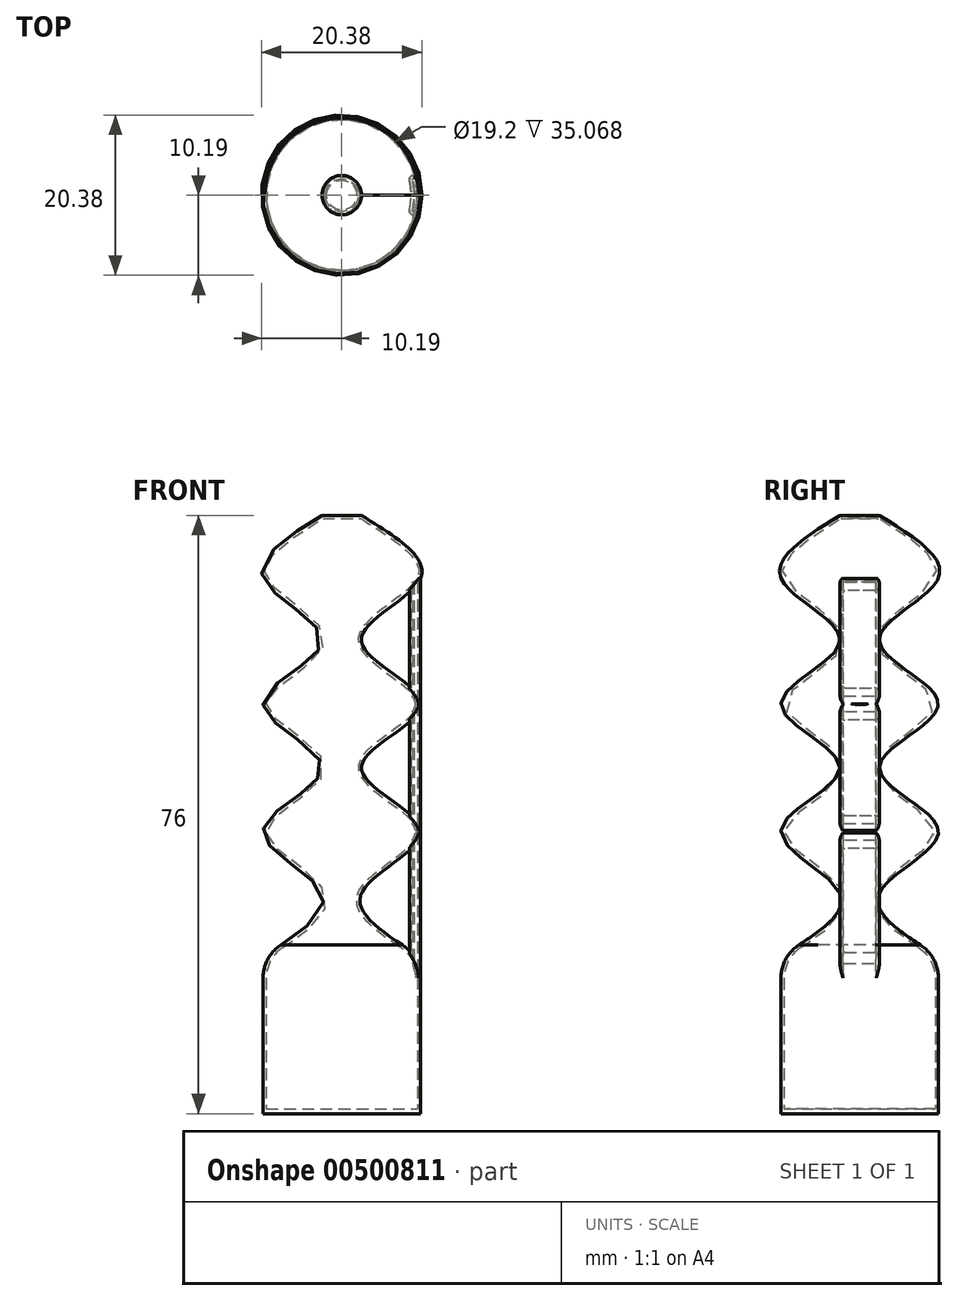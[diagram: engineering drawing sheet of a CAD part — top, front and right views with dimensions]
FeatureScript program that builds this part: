
annotation { "Feature Type Name" : "Feature", "Feature Type Description" : "" }
export const myFeature = defineFeature(function(context is Context, id is Id, definition is map)
    precondition{}
    {
        {
            var Q0;
            Q0=qCreatedBy(makeId("Top.planeOp"),FACE);
            var sketch = newSketch(context, id + "F0", { "sketchPlane" : qUnion([Q0])});
            skCircle(sketch, "E0", {"center": v(0, 0) * mm, "radius": 10 * mm});
            skSolve(sketch);
        }
        {
            var Q0;
            Q0 = qSketchRegion(id + "F0", true);
            extrude(context, id + "F1", {"entities" : qUnion([Q0]), "depth" : 20 * mm, "offsetDistance" : 25 * mm});
        }
        {
            var Q0;
            Q0=qCreatedBy(makeId("Top.planeOp"),FACE);
            cPlane(context, id + "F2", {"entities" : qUnion([Q0]), "cplaneType" : CPlaneType.OFFSET, "offset" : 20 * mm, "width" : 150 * mm, "height" : 150 * mm});
        }
        {
            var Q0;
            Q0=qCreatedBy(id+"F2.planeOp",FACE);
            cPlane(context, id + "F3", {"entities" : qUnion([Q0]), "cplaneType" : CPlaneType.OFFSET, "offset" : 8 * mm, "width" : 150 * mm, "height" : 150 * mm});
        }
        {
            var Q0;
            Q0=qCreatedBy(id+"F3.planeOp",FACE);
            cPlane(context, id + "F4", {"entities" : qUnion([Q0]), "cplaneType" : CPlaneType.OFFSET, "offset" : 8 * mm, "width" : 150 * mm, "height" : 150 * mm});
        }
        {
            var Q0;
            Q0=qCreatedBy(id+"F4.planeOp",FACE);
            cPlane(context, id + "F5", {"entities" : qUnion([Q0]), "cplaneType" : CPlaneType.OFFSET, "offset" : 8 * mm, "width" : 150 * mm, "height" : 150 * mm});
        }
        {
            var Q0;
            Q0=qCreatedBy(id+"F5.planeOp",FACE);
            cPlane(context, id + "F6", {"entities" : qUnion([Q0]), "cplaneType" : CPlaneType.OFFSET, "offset" : 8 * mm, "width" : 150 * mm, "height" : 150 * mm});
        }
        {
            var Q0;
            Q0=qCreatedBy(id+"F6.planeOp",FACE);
            cPlane(context, id + "F7", {"entities" : qUnion([Q0]), "cplaneType" : CPlaneType.OFFSET, "offset" : 8 * mm, "width" : 150 * mm, "height" : 150 * mm});
        }
        {
            var Q0;
            Q0=qCreatedBy(id+"F7.planeOp",FACE);
            cPlane(context, id + "F8", {"entities" : qUnion([Q0]), "cplaneType" : CPlaneType.OFFSET, "offset" : 8 * mm, "width" : 150 * mm, "height" : 150 * mm});
        }
        {
            var Q0;
            Q0=qCreatedBy(id+"F8.planeOp",FACE);
            cPlane(context, id + "F9", {"entities" : qUnion([Q0]), "cplaneType" : CPlaneType.OFFSET, "offset" : 8 * mm, "width" : 150 * mm, "height" : 150 * mm});
        }
        {
            var Q0;
            Q0=qCreatedBy(id+"F2.planeOp",FACE);
            var sketch = newSketch(context, id + "F10", { "sketchPlane" : qUnion([Q0])});
            skCircle(sketch, "E1", {"center": v(0, 0) * mm, "radius": 10 * mm});
            skSolve(sketch);
        }
        {
            var Q0;
            Q0=qCreatedBy(id+"F3.planeOp",FACE);
            var sketch = newSketch(context, id + "F11", { "sketchPlane" : qUnion([Q0])});
            skCircle(sketch, "E2", {"center": v(0, 0) * mm, "radius": 2.5 * mm});
            skSolve(sketch);
        }
        {
            var Q0;
            Q0=qCreatedBy(id+"F4.planeOp",FACE);
            var sketch = newSketch(context, id + "F12", { "sketchPlane" : qUnion([Q0])});
            skCircle(sketch, "E3.0", {"center": v(0, 0) * mm, "radius": 10 * mm});
            skSolve(sketch);
        }
        {
            var Q0;
            Q0=qCreatedBy(id+"F5.planeOp",FACE);
            var sketch = newSketch(context, id + "F13", { "sketchPlane" : qUnion([Q0])});
            skCircle(sketch, "E4.0", {"center": v(0, 0) * mm, "radius": 2.5 * mm});
            skSolve(sketch);
        }
        {
            var Q0;
            Q0=qCreatedBy(id+"F6.planeOp",FACE);
            var sketch = newSketch(context, id + "F14", { "sketchPlane" : qUnion([Q0])});
            skCircle(sketch, "E5.0", {"center": v(0, 0) * mm, "radius": 10 * mm});
            skSolve(sketch);
        }
        {
            var Q0;
            Q0=qCreatedBy(id+"F7.planeOp",FACE);
            var sketch = newSketch(context, id + "F15", { "sketchPlane" : qUnion([Q0])});
            skCircle(sketch, "E6.0", {"center": v(0, 0) * mm, "radius": 2.5 * mm});
            skSolve(sketch);
        }
        {
            var Q0;
            Q0=qCreatedBy(id+"F8.planeOp",FACE);
            var sketch = newSketch(context, id + "F16", { "sketchPlane" : qUnion([Q0])});
            skCircle(sketch, "E7.0", {"center": v(0, 0) * mm, "radius": 10 * mm});
            skSolve(sketch);
        }
        {
            var Q0;
            Q0=qCreatedBy(id+"F9.planeOp",FACE);
            var sketch = newSketch(context, id + "F17", { "sketchPlane" : qUnion([Q0])});
            skCircle(sketch, "E8.0", {"center": v(0, 0) * mm, "radius": 2.5 * mm});
            skSolve(sketch);
        }
        {
            var Q1;
            Q1 = qSketchRegion(id + "F10", true);
            var Q2;
            Q2 = qSketchRegion(id + "F11", true);
            var Q3;
            Q3 = qSketchRegion(id + "F12", true);
            var Q4;
            Q4 = qSketchRegion(id + "F13", true);
            var Q5;
            Q5 = qSketchRegion(id + "F14", true);
            var Q6;
            Q6 = qSketchRegion(id + "F15", true);
            var Q7;
            Q7 = qSketchRegion(id + "F16", true);
            var Q8;
            Q8 = qSketchRegion(id + "F17", true);
            loft(context, id + "F18", {"operationType" : NewBodyOperationType.ADD, "sheetProfilesArray" : [{ "sheetProfileEntities" : qUnion([Q1]) }, { "sheetProfileEntities" : qUnion([Q2]) }, { "sheetProfileEntities" : qUnion([Q3]) }, { "sheetProfileEntities" : qUnion([Q4]) }, { "sheetProfileEntities" : qUnion([Q5]) }, { "sheetProfileEntities" : qUnion([Q6]) }, { "sheetProfileEntities" : qUnion([Q7]) }, { "sheetProfileEntities" : qUnion([Q8]) }]});
        }
        {
            var Q0;
            Q0=makeQuery(id+"F18.boolean.opBoolean","MERGE",EDGE,{"derivedFrom":[makeQuery(id+"F1.opExtrude","CAP_EDGE",EDGE,{"disambiguationData":[OSD([sQuery(id+"F0.wireOp",EDGE,"E0")])],"isStart":false}),makeQuery(id+"F18.opLoft","MID_CAP_EDGE",EDGE,{"disambiguationData":[OSD([sQuery(id+"F10.wireOp",EDGE,"E1")])],"capPos":0.0})]});
            fillet(context, id + "F19", {"entities" : qUnion([Q0]), "radius" : 5 * mm, "tangentPropagation" : true, "allowEdgeOverflow" : false});
        }
        {
            var Q0;
            Q0=makeQuery(id+"F1.opExtrude","CAP_FACE",FACE,{"disambiguationData":[OSD([sQuery(id+"F0.wireOp",EDGE,"E0")])],"isStart":true});
            var sketch = newSketch(context, id + "F20", { "sketchPlane" : qUnion([Q0])});
            skArc(sketch, "E9.0", {"start": v(9.78, -2.1) * mm, "mid": v(10, 0) * mm, "end": v(9.78, 2.1) * mm});
            skLineSegment(sketch, "E10", {"start": v(9.08, 2.5) * mm, "end": v(9.29, 2.5) * mm});
            skArc(sketch, "E11.0", {"start": v(8.6, -1.9) * mm, "mid": v(8.8, 0) * mm, "end": v(8.6, 1.9) * mm});
            skLineSegment(sketch, "E12", {"start": v(9.08, -2.5) * mm, "end": v(9.29, -2.5) * mm});
            skPoint(sketch, "E13.visualSharp", {"position": v(8.44, 2.5) * mm});
            skArc(sketch, "E13.filletArc", {"start": v(9.08, 2.5) * mm, "mid": v(8.7, 2.31) * mm, "end": v(8.6, 1.9) * mm});
            skPoint(sketch, "E14.visualSharp", {"position": v(8.44, -2.5) * mm});
            skArc(sketch, "E14.filletArc", {"start": v(8.6, -1.9) * mm, "mid": v(8.7, -2.31) * mm, "end": v(9.08, -2.5) * mm});
            skPoint(sketch, "E15.visualSharp", {"position": v(9.68, 2.5) * mm});
            skArc(sketch, "E15.filletArc", {"start": v(9.78, 2.1) * mm, "mid": v(9.6, 2.39) * mm, "end": v(9.29, 2.5) * mm});
            skPoint(sketch, "E16.visualSharp", {"position": v(9.68, -2.5) * mm});
            skArc(sketch, "E16.filletArc", {"start": v(9.29, -2.5) * mm, "mid": v(9.6, -2.39) * mm, "end": v(9.78, -2.1) * mm});
            skSolve(sketch);
        }
        {
            var Q0;
            Q0 = qSketchRegion(id + "F20", true);
            extrude(context, id + "F21", {"entities" : qUnion([Q0]), "operationType" : NewBodyOperationType.ADD, "oppositeDirection" : true, "depth" : 68 * mm, "offsetDistance" : 25 * mm});
        }
        {
            var Q0;
            Q0=makeQuery(id+"F1.opExtrude","CAP_FACE",FACE,{"disambiguationData":[OSD([sQuery(id+"F0.wireOp",EDGE,"E0")])],"isStart":true});
            shell(context, id + "F22", {"entities" : qUnion([Q0]), "thickness" : .4 * mm});
        }
        {
            var Q0;
            Q0=makeQuery(id+"F1.opExtrude","CAP_FACE",FACE,{"disambiguationData":[OSD([sQuery(id+"F0.wireOp",EDGE,"E0")])],"isStart":true});
            var sketch = newSketch(context, id + "F23", { "sketchPlane" : qUnion([Q0])});
            skCircle(sketch, "E17", {"center": v(0, 0) * mm, "radius": 10 * mm});
            skSolve(sketch);
        }
        {
            var Q0;
            Q0 = qSketchRegion(id + "F23", true);
            extrude(context, id + "F24", {"entities" : qUnion([Q0]), "operationType" : NewBodyOperationType.ADD, "oppositeDirection" : true, "depth" : .6 * mm, "offsetDistance" : 25 * mm});
        }
    });
